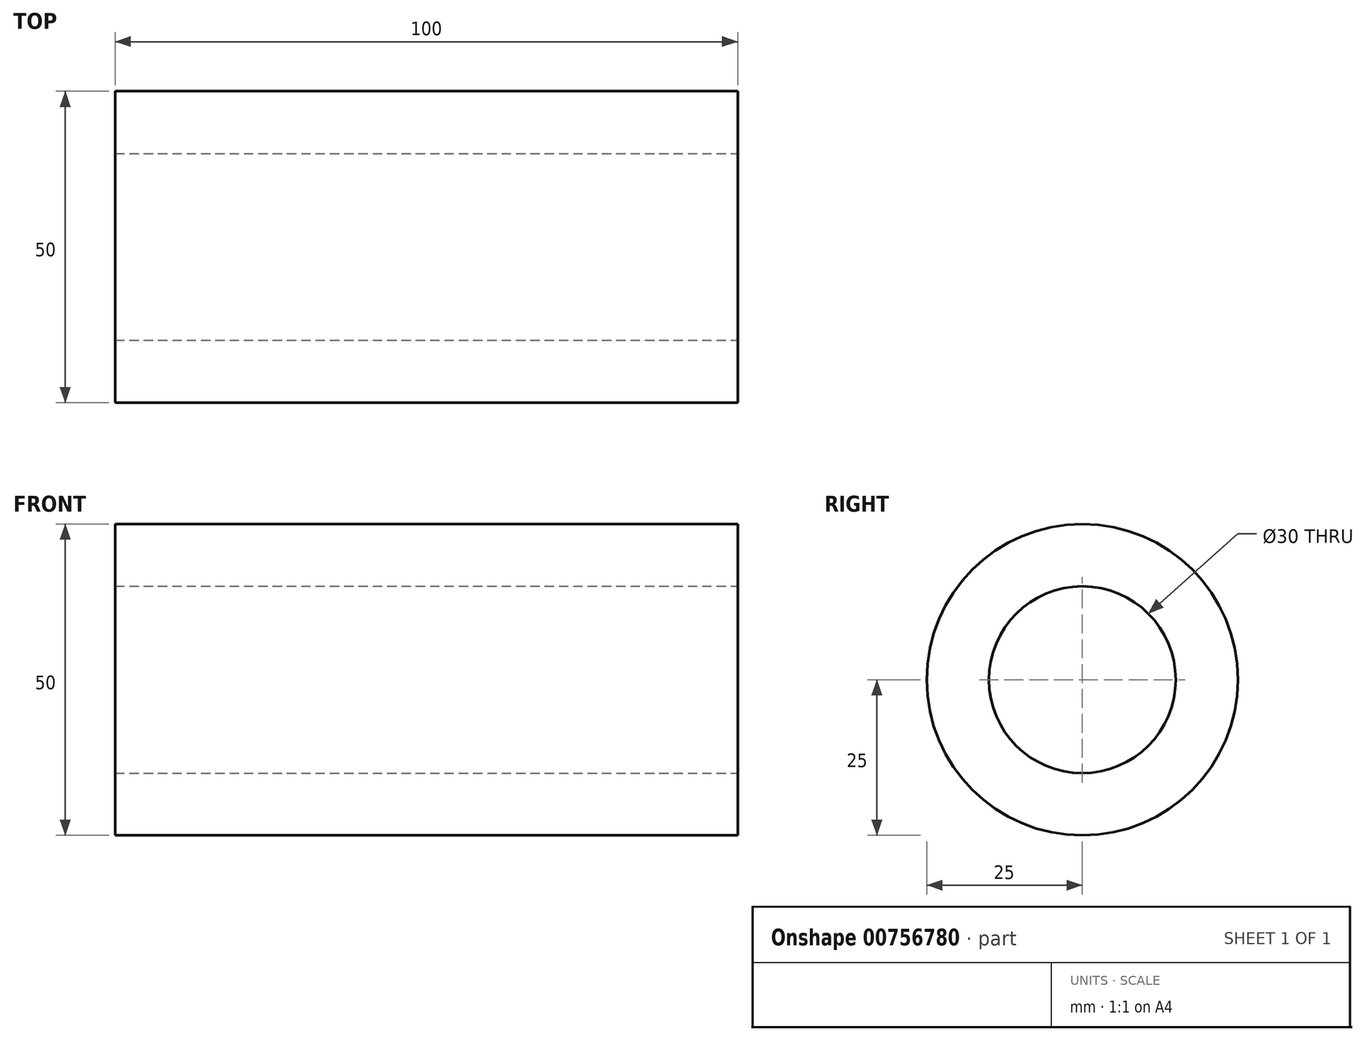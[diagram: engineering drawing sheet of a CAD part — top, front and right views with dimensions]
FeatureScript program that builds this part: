
annotation { "Feature Type Name" : "Feature", "Feature Type Description" : "" }
export const myFeature = defineFeature(function(context is Context, id is Id, definition is map)
    precondition{}
    {
        {
            var Q0;
            Q0=qCreatedBy(makeId("Right.planeOp"),FACE);
            var sketch = newSketch(context, id + "F0", { "sketchPlane" : qUnion([Q0])});
            skCircle(sketch, "E0", {"center": v(0, 0) * mm, "radius": 25 * mm});
            skSolve(sketch);
        }
        {
            var Q0;
            Q0=makeQuery(id+"F0.imprint","IMPRINT",FACE,{"disambiguationData":[TD([[makeQuery(id+"F0.imprint","IMPRINT",EDGE,{"derivedFrom":sQuery(id+"F0.wireOp",EDGE,"E0")}),1.0]])]});
            extrude(context, id + "F1", {"entities" : qUnion([Q0]), "depth" : 100 * mm, "offsetDistance" : 25 * mm});
        }
        {
            var Q0;
            Q0=makeQuery(id+"F1.opExtrude","CAP_FACE",FACE,{"disambiguationData":[OSD([sQuery(id+"F0.wireOp",EDGE,"E0")])],"isStart":false});
            var sketch = newSketch(context, id + "F2", { "sketchPlane" : qUnion([Q0])});
            skCircle(sketch, "E1", {"center": v(0, 0) * mm, "radius": 15 * mm});
            skSolve(sketch);
        }
        {
            var Q0;
            Q0=makeQuery(id+"F2.imprint","IMPRINT",FACE,{"disambiguationData":[TD([[makeQuery(id+"F2.imprint","IMPRINT",EDGE,{"derivedFrom":sQuery(id+"F2.wireOp",EDGE,"E1")}),1.0]])]});
            extrude(context, id + "F3", {"entities" : qUnion([Q0]), "operationType" : NewBodyOperationType.REMOVE, "endBound" : BoundingType.THROUGH_ALL, "oppositeDirection" : true, "depth" : 25 * mm, "offsetDistance" : 25 * mm});
        }
    });
